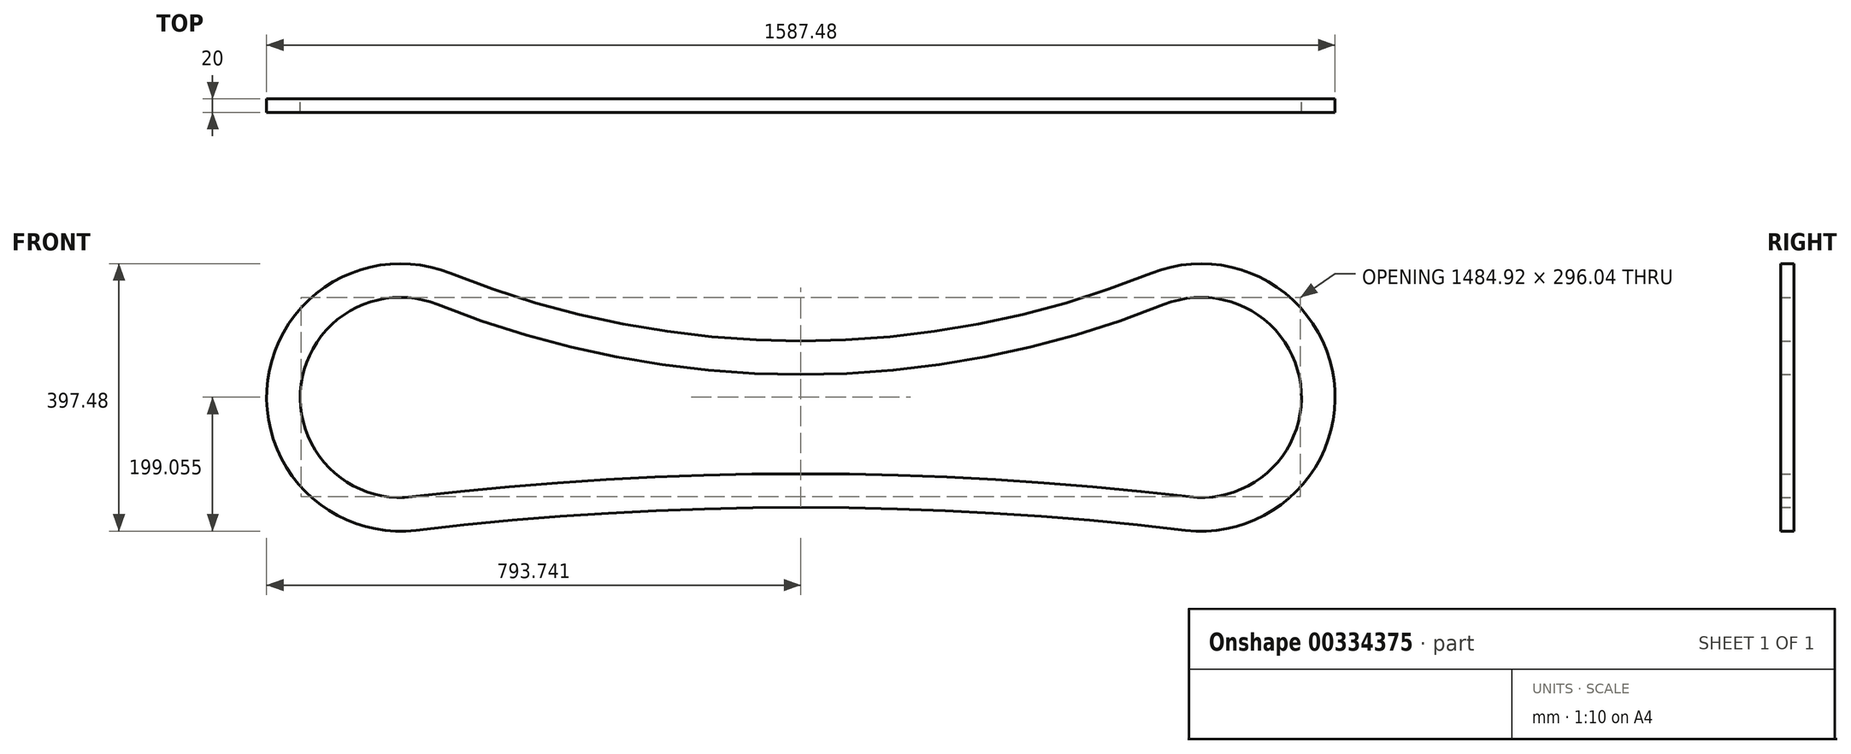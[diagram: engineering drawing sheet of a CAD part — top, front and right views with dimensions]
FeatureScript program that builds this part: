
annotation { "Feature Type Name" : "Feature", "Feature Type Description" : "" }
export const myFeature = defineFeature(function(context is Context, id is Id, definition is map)
    precondition{}
    {
        {
            var Q0;
            Q0=qCreatedBy(makeId("Front.planeOp"),FACE);
            var sketch = newSketch(context, id + "F0", { "sketchPlane" : qUnion([Q0])});
            skArc(sketch, "E0", {"start": v(-526.25, 184.48) * mm, "mid": v(-797.2, 26.06) * mm, "end": v(-576.76, -197.36) * mm});
            skArc(sketch, "E1", {"start": v(566.4, -197.36) * mm, "mid": v(786.85, 26.06) * mm, "end": v(515.89, 184.48) * mm});
            skLineSegment(sketch, "E2", {"start": v(-600.18, 0) * mm, "end": v(589.82, 0) * mm});
            skArc(sketch, "E3", {"start": v(566.4, -197.36) * mm, "mid": v(-5.18, -163.56) * mm, "end": v(-576.76, -197.36) * mm});
            skPoint(sketch, "E3.centerSnap0", {"position": v(-5.18, 0) * mm});
            skArc(sketch, "E4", {"start": v(-526.25, 184.48) * mm, "mid": v(-5.18, 83.95) * mm, "end": v(515.89, 184.48) * mm});
            skArc(sketch, "E5.0", {"start": v(-544.85, 138.07) * mm, "mid": v(-5.18, 33.95) * mm, "end": v(534.49, 138.07) * mm});
            skArc(sketch, "E6.0", {"start": v(-544.85, 138.07) * mm, "mid": v(-747.64, 19.5) * mm, "end": v(-582.65, -147.7) * mm});
            skArc(sketch, "E7.0", {"start": v(572.3, -147.7) * mm, "mid": v(737.28, 19.5) * mm, "end": v(534.49, 138.07) * mm});
            skArc(sketch, "E8.0", {"start": v(572.3, -147.7) * mm, "mid": v(-5.18, -113.56) * mm, "end": v(-582.65, -147.7) * mm});
            skSolve(sketch);
        }
        {
            var Q0;
            Q0=makeQuery(id+"F0.imprint","IMPRINT",FACE,{"disambiguationData":[TD([[makeQuery(id+"F0.imprint","IMPRINT",EDGE,{"derivedFrom":sQuery(id+"F0.wireOp",EDGE,"E0")}),1.0]])]});
            extrude(context, id + "F1", {"entities" : qUnion([Q0]), "depth" : 20 * mm});
        }
    });
